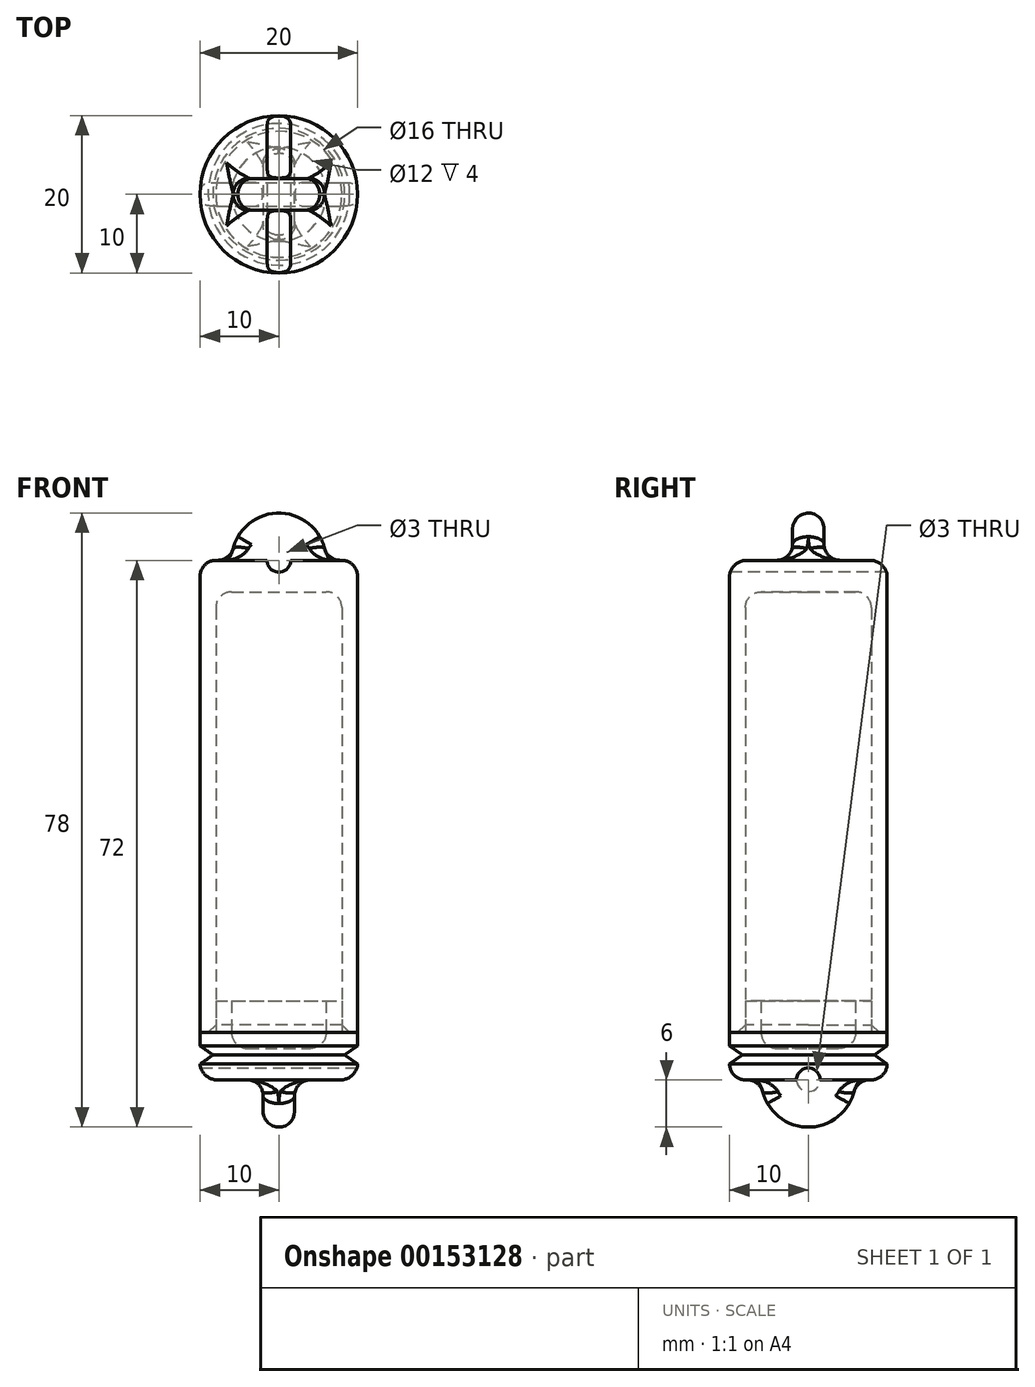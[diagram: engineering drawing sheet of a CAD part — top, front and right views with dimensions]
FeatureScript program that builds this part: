
annotation { "Feature Type Name" : "Feature", "Feature Type Description" : "" }
export const myFeature = defineFeature(function(context is Context, id is Id, definition is map)
    precondition{}
    {
        {
            var Q0;
            Q0=qCreatedBy(makeId("Front.planeOp"),FACE);
            var sketch = newSketch(context, id + "F0", { "sketchPlane" : qUnion([Q0])});
            skLineSegment(sketch, "E0", {"start": v(3.87, 0) * mm, "end": v(4, 0) * mm});
            skLineSegment(sketch, "E1", {"start": v(5, 2.16) * mm, "end": v(5, 5) * mm});
            skLineSegment(sketch, "E2.0", {"start": v(3, 3) * mm, "end": v(3, 5) * mm});
            skLineSegment(sketch, "E2.1", {"start": v(0, 2) * mm, "end": v(2, 2) * mm});
            skPoint(sketch, "E3.visualSharp", {"position": v(3, 2) * mm});
            skArc(sketch, "E3.filletArc", {"start": v(2, 2) * mm, "mid": v(2.7, 2.3) * mm, "end": v(3, 3) * mm});
            skLineSegment(sketch, "E4", {"start": v(3, 5) * mm, "end": v(4, 5) * mm});
            skLineSegment(sketch, "E5", {"start": v(0, 0) * mm, "end": v(0, 2) * mm});
            skLineSegment(sketch, "E6", {"start": v(5, 3) * mm, "end": v(4, 3) * mm});
            skPoint(sketch, "E7.visualSharp", {"position": v(5, 0) * mm});
            skArc(sketch, "E7.filletArc", {"start": v(4, 0) * mm, "mid": v(4.7, 0.3) * mm, "end": v(5, 1) * mm});
            skLineSegment(sketch, "E8.trimOffspring", {"start": v(4, 3) * mm, "end": v(4, 5) * mm});
            skLineSegment(sketch, "E9", {"start": v(0, 0) * mm, "end": v(0, -3) * mm});
            skArc(sketch, "E10", {"start": v(0, -3) * mm, "mid": v(1.84, -2.37) * mm, "end": v(2.9, -0.75) * mm});
            skPoint(sketch, "E11.visualSharp", {"position": v(3, 0) * mm});
            skArc(sketch, "E11.filletArc", {"start": v(3.87, 0) * mm, "mid": v(3.26, -0.2) * mm, "end": v(2.9, -0.75) * mm});
            skLineSegment(sketch, "E12", {"start": v(5, 1) * mm, "end": v(4.19, 1.58) * mm});
            skLineSegment(sketch, "E13", {"start": v(4.19, 1.58) * mm, "end": v(5, 2.16) * mm});
            skSolve(sketch);
        }
        {
            var Q0;
            Q0 = qSketchRegion(id + "F0", true);
            var Q1;
            Q1=sQuery(id+"F0.wireOp",EDGE,"E5");
            revolve(context, id + "F1", {"entities" : qUnion([Q0]), "axis" : qUnion([Q1]), "revolveType" : RevolveType.FULL});
        }
        {
            var Q0;
            Q0=qCreatedBy(makeId("Top.planeOp"),FACE);
            var sketch = newSketch(context, id + "F2", { "sketchPlane" : qUnion([Q0])});
            skLineSegment(sketch, "E14", {"start": v(0, 0) * mm, "end": v(1, 0) * mm});
            skLineSegment(sketch, "E15", {"start": v(1, 0) * mm, "end": v(1, -5) * mm});
            skLineSegment(sketch, "E16", {"start": v(1, -5) * mm, "end": v(0, -5) * mm});
            skLineSegment(sketch, "E17", {"start": v(0, -5) * mm, "end": v(0, 0) * mm});
            skLineSegment(sketch, "E18.MirrorCS", {"start": v(1, 5) * mm, "end": v(0, 5) * mm});
            skLineSegment(sketch, "E19.MirrorCS", {"start": v(0, 5) * mm, "end": v(0, 0) * mm});
            skLineSegment(sketch, "E20.MirrorCS", {"start": v(1, 0) * mm, "end": v(1, 5) * mm});
            skLineSegment(sketch, "E21.MirrorCS", {"start": v(-1, 0) * mm, "end": v(-1, 5) * mm});
            skLineSegment(sketch, "E22.MirrorCS", {"start": v(-1, 5) * mm, "end": v(0, 5) * mm});
            skLineSegment(sketch, "E23.MirrorCS", {"start": v(0, 0) * mm, "end": v(-1, 0) * mm});
            skLineSegment(sketch, "E24.MirrorCS", {"start": v(-1, 0) * mm, "end": v(-1, -5) * mm});
            skLineSegment(sketch, "E25.MirrorCS", {"start": v(-1, -5) * mm, "end": v(0, -5) * mm});
            skLineSegment(sketch, "E26", {"start": v(-1, -5) * mm, "end": v(-5.22, -5) * mm});
            skLineSegment(sketch, "E27", {"start": v(-5.22, -5) * mm, "end": v(-5.22, 5) * mm});
            skLineSegment(sketch, "E28", {"start": v(-1, 5) * mm, "end": v(-5.22, 5) * mm});
            skLineSegment(sketch, "E29.MirrorCS", {"start": v(1, 5) * mm, "end": v(5.22, 5) * mm});
            skLineSegment(sketch, "E30.MirrorCS", {"start": v(5.22, -5) * mm, "end": v(5.22, 5) * mm});
            skLineSegment(sketch, "E31.MirrorCS", {"start": v(1, -5) * mm, "end": v(5.22, -5) * mm});
            skSolve(sketch);
        }
        {
            var Q0;
            Q0=makeQuery(id+"F2.imprint","IMPRINT",FACE,{"disambiguationData":[TD([[makeQuery(id+"F2.imprint","IMPRINT",EDGE,{"derivedFrom":sQuery(id+"F2.wireOp",EDGE,"E21.MirrorCS")}),1.0]])]});
            var Q1;
            Q1=makeQuery(id+"F2.imprint","IMPRINT",FACE,{"disambiguationData":[TD([[makeQuery(id+"F2.imprint","IMPRINT",EDGE,{"derivedFrom":sQuery(id+"F2.wireOp",EDGE,"E20.MirrorCS")}),-1.0]])]});
            extrude(context, id + "F3", {"entities" : qUnion([Q0, Q1]), "operationType" : NewBodyOperationType.REMOVE, "oppositeDirection" : true, "depth" : 25 * mm});
        }
        {
            var Q0;
            Q0=makeQuery(id+"F3.boolean.opBoolean","COPY",EDGE,{"derivedFrom":makeQuery(id+"F3.opExtrude","CAP_EDGE",EDGE,{"disambiguationData":[OSD([sQuery(id+"F2.wireOp",EDGE,"E20.MirrorCS"),sQuery(id+"F2.wireOp",EDGE,"E15")])],"isStart":true})});
            var Q1;
            Q1=makeQuery(id+"F3.boolean.opBoolean","COPY",EDGE,{"derivedFrom":makeQuery(id+"F3.opExtrude","CAP_EDGE",EDGE,{"disambiguationData":[OSD([sQuery(id+"F2.wireOp",EDGE,"E21.MirrorCS"),sQuery(id+"F2.wireOp",EDGE,"E24.MirrorCS")])],"isStart":true})});
            fillet(context, id + "F4", {"entities" : qUnion([Q0, Q1]), "radius" : 1 * mm, "tangentPropagation" : true, "allowEdgeOverflow" : false});
        }
        {
            var Q0;
            Q0=makeQuery(id+"F3.boolean.opBoolean","COPY",FACE,{"derivedFrom":makeQuery(id+"F3.opExtrude","SWEPT_FACE",FACE,{"disambiguationData":[OSD([sQuery(id+"F2.wireOp",EDGE,"E20.MirrorCS"),sQuery(id+"F2.wireOp",EDGE,"E15")])]})});
            var sketch = newSketch(context, id + "F5", { "sketchPlane" : qUnion([Q0])});
            skArc(sketch, "E32.0", {"start": v(1.71, -0.65) * mm, "mid": v(0, -1.83) * mm, "end": v(-1.71, -0.65) * mm});
            skCircle(sketch, "E33", {"center": v(0, 0) * mm, "radius": 0.75 * mm});
            skSolve(sketch);
        }
        {
            var Q0;
            Q0 = qSketchRegion(id + "F5", true);
            extrude(context, id + "F6", {"entities" : qUnion([Q0]), "operationType" : NewBodyOperationType.REMOVE, "endBound" : BoundingType.SYMMETRIC, "oppositeDirection" : true, "depth" : 25 * mm});
        }
        {
            var Q0;
            Q0=makeQuery(id+"F3.boolean.opBoolean","INTERSECT",EDGE,{"derivedFrom":[makeQuery(id+"F1.opRevolve","SWEPT_FACE",FACE,{"disambiguationData":[OSD([sQuery(id+"F0.wireOp",EDGE,"E10")])]}),makeQuery(id+"F3.opExtrude","SWEPT_FACE",FACE,{"disambiguationData":[OSD([sQuery(id+"F2.wireOp",EDGE,"E21.MirrorCS"),sQuery(id+"F2.wireOp",EDGE,"E24.MirrorCS")])]})]});
            var Q1;
            Q1=makeQuery(id+"F3.boolean.opBoolean","INTERSECT",EDGE,{"derivedFrom":[makeQuery(id+"F1.opRevolve","SWEPT_FACE",FACE,{"disambiguationData":[OSD([sQuery(id+"F0.wireOp",EDGE,"E10")])]}),makeQuery(id+"F3.opExtrude","SWEPT_FACE",FACE,{"disambiguationData":[OSD([sQuery(id+"F2.wireOp",EDGE,"E20.MirrorCS"),sQuery(id+"F2.wireOp",EDGE,"E15")])]})]});
            fillet(context, id + "F7", {"entities" : qUnion([Q0, Q1]), "radius" : 1 * mm, "tangentPropagation" : true, "allowEdgeOverflow" : false});
        }
        {
            var Q0;
            Q0=makeQuery(id+"F1.opRevolve","SWEPT_FACE",FACE,{"disambiguationData":[OSD([sQuery(id+"F0.wireOp",EDGE,"E6")])]});
            extrude(context, id + "F8", {"entities" : qUnion([Q0]), "depth" : 25 * mm});
        }
        {
            var Q0;
            Q0=makeQuery(id+"F8.opExtrude","CAP_FACE",FACE,{"disambiguationData":[OSD([sQuery(id+"F0.wireOp",EDGE,"E6")])],"isStart":false});
            var sketch = newSketch(context, id + "F9", { "sketchPlane" : qUnion([Q0])});
            skLineSegment(sketch, "E34", {"start": v(0, 0) * mm, "end": v(0, 5) * mm});
            skSolve(sketch);
        }
        {
            var Q0;
            Q0=qCreatedBy(makeId("Right.planeOp"),FACE);
            var sketch = newSketch(context, id + "F10", { "sketchPlane" : qUnion([Q0])});
            skLineSegment(sketch, "E35", {"start": v(5, 28) * mm, "end": v(5, 32) * mm});
            skLineSegment(sketch, "E36", {"start": v(4, 33) * mm, "end": v(3.87, 33) * mm});
            skLineSegment(sketch, "E37.1", {"start": v(4, 28) * mm, "end": v(4, 30) * mm});
            skPoint(sketch, "E38.visualSharp", {"position": v(5, 33) * mm});
            skArc(sketch, "E38.filletArc", {"start": v(5, 32) * mm, "mid": v(4.7, 32.7) * mm, "end": v(4, 33) * mm});
            skLineSegment(sketch, "E39", {"start": v(0, 33) * mm, "end": v(0, 36) * mm});
            skArc(sketch, "E40", {"start": v(2.9, 33.75) * mm, "mid": v(1.84, 35.37) * mm, "end": v(0, 36) * mm});
            skLineSegment(sketch, "E41", {"start": v(5, 33) * mm, "end": v(5, 31) * mm});
            skLineSegment(sketch, "E42", {"start": v(3, 31) * mm, "end": v(0, 31) * mm});
            skPoint(sketch, "E43.visualSharp", {"position": v(4, 31) * mm});
            skArc(sketch, "E43.filletArc", {"start": v(4, 30) * mm, "mid": v(3.7, 30.7) * mm, "end": v(3, 31) * mm});
            skPoint(sketch, "E44.visualSharp", {"position": v(3, 33) * mm});
            skArc(sketch, "E44.filletArc", {"start": v(2.9, 33.75) * mm, "mid": v(3.26, 33.2) * mm, "end": v(3.87, 33) * mm});
            skLineSegment(sketch, "E45", {"start": v(0, 31) * mm, "end": v(0, 36) * mm});
            skLineSegment(sketch, "E46", {"start": v(4, 28) * mm, "end": v(5, 28) * mm});
            skSolve(sketch);
        }
        {
            var Q0;
            Q0 = qSketchRegion(id + "F10", true);
            var Q1;
            Q1=sQuery(id+"F10.wireOp",EDGE,"E45");
            revolve(context, id + "F11", {"operationType" : NewBodyOperationType.ADD, "entities" : qUnion([Q0]), "axis" : qUnion([Q1]), "revolveType" : RevolveType.FULL});
        }
        {
            var Q0;
            Q0=qCreatedBy(makeId("Top.planeOp"),FACE);
            var sketch = newSketch(context, id + "F12", { "sketchPlane" : qUnion([Q0])});
            skLineSegment(sketch, "E47", {"start": v(0, 0) * mm, "end": v(0, 1) * mm});
            skLineSegment(sketch, "E48", {"start": v(0, 1) * mm, "end": v(6, 1) * mm});
            skLineSegment(sketch, "E49", {"start": v(6, 1) * mm, "end": v(6, 0) * mm});
            skLineSegment(sketch, "E50", {"start": v(6, 0) * mm, "end": v(0, 0) * mm});
            skLineSegment(sketch, "E51", {"start": v(6, 0) * mm, "end": v(8.51, 0) * mm});
            skLineSegment(sketch, "E52", {"start": v(8.51, 0) * mm, "end": v(8.51, 5.7) * mm});
            skLineSegment(sketch, "E53", {"start": v(8.51, 5.7) * mm, "end": v(0, 5.7) * mm});
            skLineSegment(sketch, "E54", {"start": v(0, 5.7) * mm, "end": v(0, 1) * mm});
            skLineSegment(sketch, "E55.MirrorCS", {"start": v(-8.51, 5.7) * mm, "end": v(0, 5.7) * mm});
            skLineSegment(sketch, "E56.MirrorCS", {"start": v(-8.51, 0) * mm, "end": v(-8.51, 5.7) * mm});
            skLineSegment(sketch, "E57.MirrorCS", {"start": v(-6, 0) * mm, "end": v(-8.51, 0) * mm});
            skLineSegment(sketch, "E58.MirrorCS", {"start": v(-6, 0) * mm, "end": v(0, 0) * mm});
            skLineSegment(sketch, "E59.MirrorCS", {"start": v(-6, 1) * mm, "end": v(-6, 0) * mm});
            skLineSegment(sketch, "E60.MirrorCS", {"start": v(0, 1) * mm, "end": v(-6, 1) * mm});
            skLineSegment(sketch, "E61.MirrorCS", {"start": v(8.51, 0) * mm, "end": v(8.51, -5.7) * mm});
            skLineSegment(sketch, "E62.MirrorCS", {"start": v(8.51, -5.7) * mm, "end": v(0, -5.7) * mm});
            skLineSegment(sketch, "E63.MirrorCS", {"start": v(-8.51, -5.7) * mm, "end": v(0, -5.7) * mm});
            skLineSegment(sketch, "E64.MirrorCS", {"start": v(-8.51, 0) * mm, "end": v(-8.51, -5.7) * mm});
            skLineSegment(sketch, "E65.MirrorCS", {"start": v(0, -1) * mm, "end": v(-6, -1) * mm});
            skLineSegment(sketch, "E66.MirrorCS", {"start": v(0, -1) * mm, "end": v(6, -1) * mm});
            skLineSegment(sketch, "E67.MirrorCS", {"start": v(6, -1) * mm, "end": v(6, 0) * mm});
            skLineSegment(sketch, "E68.MirrorCS", {"start": v(-6, -1) * mm, "end": v(-6, 0) * mm});
            skSolve(sketch);
        }
        {
            var Q0;
            Q0 = qSketchRegion(id + "F12", true);
            extrude(context, id + "F13", {"entities" : qUnion([Q0]), "operationType" : NewBodyOperationType.REMOVE, "depth" : 38.3 * mm, "hasSecondDirection" : true, "secondDirectionOppositeDirection" : false, "secondDirectionDepth" : 33 * mm});
        }
        {
            var Q0;
            Q0=makeQuery(id+"F13.boolean.opBoolean","COPY",EDGE,{"derivedFrom":makeQuery(id+"F13.opExtrude","CAP_EDGE",EDGE,{"disambiguationData":[OSD([sQuery(id+"F12.wireOp",EDGE,"E65.MirrorCS"),sQuery(id+"F12.wireOp",EDGE,"E66.MirrorCS")])],"isStart":true})});
            var Q1;
            Q1=makeQuery(id+"F13.boolean.opBoolean","COPY",EDGE,{"derivedFrom":makeQuery(id+"F13.opExtrude","CAP_EDGE",EDGE,{"disambiguationData":[OSD([sQuery(id+"F12.wireOp",EDGE,"E48"),sQuery(id+"F12.wireOp",EDGE,"E60.MirrorCS")])],"isStart":true})});
            fillet(context, id + "F14", {"entities" : qUnion([Q0, Q1]), "radius" : 1 * mm, "tangentPropagation" : true, "allowEdgeOverflow" : false});
        }
        {
            var Q0;
            Q0=makeQuery(id+"F13.boolean.opBoolean","INTERSECT",EDGE,{"derivedFrom":[makeQuery(id+"F11.opRevolve","SWEPT_FACE",FACE,{"disambiguationData":[OSD([sQuery(id+"F10.wireOp",EDGE,"E40")])]}),makeQuery(id+"F13.opExtrude","SWEPT_FACE",FACE,{"disambiguationData":[OSD([sQuery(id+"F12.wireOp",EDGE,"E65.MirrorCS"),sQuery(id+"F12.wireOp",EDGE,"E66.MirrorCS")])]})]});
            var Q1;
            Q1=makeQuery(id+"F13.boolean.opBoolean","INTERSECT",EDGE,{"derivedFrom":[makeQuery(id+"F11.opRevolve","SWEPT_FACE",FACE,{"disambiguationData":[OSD([sQuery(id+"F10.wireOp",EDGE,"E40")])]}),makeQuery(id+"F13.opExtrude","SWEPT_FACE",FACE,{"disambiguationData":[OSD([sQuery(id+"F12.wireOp",EDGE,"E48"),sQuery(id+"F12.wireOp",EDGE,"E60.MirrorCS")])]})]});
            fillet(context, id + "F15", {"entities" : qUnion([Q0, Q1]), "radius" : 1 * mm, "tangentPropagation" : true, "allowEdgeOverflow" : false});
        }
        {
            var Q0;
            Q0=makeQuery(id+"F13.boolean.opBoolean","COPY",FACE,{"derivedFrom":makeQuery(id+"F13.opExtrude","SWEPT_FACE",FACE,{"disambiguationData":[OSD([sQuery(id+"F12.wireOp",EDGE,"E65.MirrorCS"),sQuery(id+"F12.wireOp",EDGE,"E66.MirrorCS")])]})});
            var sketch = newSketch(context, id + "F16", { "sketchPlane" : qUnion([Q0])});
            skArc(sketch, "E69.0", {"start": v(0.87, 33.5) * mm, "mid": v(0, 34) * mm, "end": v(-0.87, 33.5) * mm});
            skCircle(sketch, "E70", {"center": v(0, 33) * mm, "radius": 0.75 * mm});
            skSolve(sketch);
        }
        {
            var Q0;
            Q0 = qSketchRegion(id + "F16", true);
            extrude(context, id + "F17", {"entities" : qUnion([Q0]), "operationType" : NewBodyOperationType.REMOVE, "endBound" : BoundingType.SYMMETRIC, "oppositeDirection" : true, "depth" : 25 * mm});
        }
        {
            var Q0;
            Q0=makeQuery(id+"F8.opExtrude","CAP_EDGE",EDGE,{"disambiguationData":[OSD([sQuery(id+"F0.wireOp",EDGE,"E6"),sQuery(id+"F0.wireOp",EDGE,"E8.trimOffspring")])],"isStart":true});
            chamfer(context, id + "F18", {"entities" : qUnion([Q0]), "width" : .5 * mm, "tangentPropagation" : true});
        }
        {
            var Q0;
            Q0=makeQuery(id+"F8.opExtrude","SWEPT_BODY",BODY,{"disambiguationData":[OSD([sQuery(id+"F0.wireOp",EDGE,"E6")])]});
            var Q1;
            Q1=makeQuery(id+"F1.opRevolve","SWEPT_BODY",BODY,{"disambiguationData":[OSD([sQuery(id+"F0.wireOp",EDGE,"E0"),sQuery(id+"F0.wireOp",EDGE,"E1"),sQuery(id+"F0.wireOp",EDGE,"E2.0"),sQuery(id+"F0.wireOp",EDGE,"E2.1"),sQuery(id+"F0.wireOp",EDGE,"E3.filletArc"),sQuery(id+"F0.wireOp",EDGE,"E4"),sQuery(id+"F0.wireOp",EDGE,"E5"),sQuery(id+"F0.wireOp",EDGE,"E6"),sQuery(id+"F0.wireOp",EDGE,"E7.filletArc"),sQuery(id+"F0.wireOp",EDGE,"E8.trimOffspring"),sQuery(id+"F0.wireOp",EDGE,"E9"),sQuery(id+"F0.wireOp",EDGE,"E10"),sQuery(id+"F0.wireOp",EDGE,"E11.filletArc"),sQuery(id+"F0.wireOp",EDGE,"E12"),sQuery(id+"F0.wireOp",EDGE,"E13")])]});
            var Q2;
            Q2=qCreatedBy(makeId("Origin.pointOp"),VERTEX);
            transform(context, id + "F19", {"entities" : qUnion([Q0, Q1]), "transformType" : TransformType.SCALE_UNIFORMLY, "scale" : 2, "scalePoint" : qUnion([Q2]), "makeCopy" : false});
        }
    });
